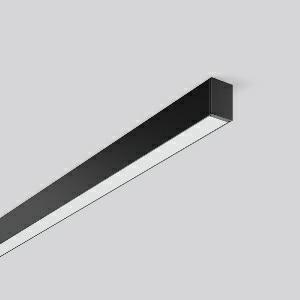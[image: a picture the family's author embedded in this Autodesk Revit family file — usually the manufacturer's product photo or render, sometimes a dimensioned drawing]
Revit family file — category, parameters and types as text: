
# Revit family: less_is_more_27_312197_003_76_2e7d
name_source: partatom
category: Lighting Fixtures
units: mm (PartAtom-declared; Revit-internal decimal feet)

## family parameters
Cut with Voids When Loaded = No
Host = Face
Light Source = No
Part Type = Normal
Room Calculation Point = No
Round Connector Dimension = Use Diameter
Shared = No

## types (1)
- LESS IS MORE 27 (1 x LED Modul 830, 1800 lm, 3000)
    Apparent Load = 29 VA
    CIE Flux Codes = 65 89 98 100 100
    Color Rendering = 80
    Color Temperature = 3000
    Default Elevation = 1800 mm  [stored 5.90551 ft]
    Description = Series: LESS IS MORE 27
Ceiling luminaire with slim design. Housing: extruded aluminium profile, powder-coated. End cap aluminium powder-coated. Diffuser made of non-yellowing plastic (PMMA) microprismatic. Suitable for Ceiling mounting, Wall (surface). External driver with connecting cable. 
Colour: deep black, matt (RAL 9005)
Length: 1012 mm
Width: 28 mm
Height: 38 mm
Lamp: LED
Socket: without socket
Colour temperature: 3000K
Colour rendering index (CRI): 82
System power: 29 W
Rated luminous flux: 1800 lm
Luminous efficiency: 62 lm/W
Control gear: Voltage converter, DALI dim.
Protection class: II
Type of protection: IP 20
    Height = 38 mm
    Lamp = 1 x LED Modul 830
    Lamp Light Flux = 1800 lm
    Lamp count = 1
    Length = 1012 mm
    Lifetime = 50000 h
    Luminous efficacy = 62 lm/W
    Manufacturer = RZB
    ModVariant = No
    Model = 312197.003.76
    Mounting Place = Ceiling, Wall
    Mounting Type = Surface mounted
    Number of Poles = 1
    OnlyDefault = Yes
    Power Factor = 1
    Product Name = LESS IS MORE 27
    Product group = Surface mounted LED linear luminaires
    ProductGroupID = 307
    Protection Class = Protection class II
    Protection Degree = IP 20
    RLX_Detail_Level = 1
    RLX_Emergency_Light_Flux = 0 lm
    RLX_Emergency_Type = 0
    RLX_Emergency_Type_DB = No
    RlxData = <blob elided: 29785 chars, md5=38d0541e>
    Socket = socket
    Standby Power = 0 W
    System Light Flux = 1800 lm
    System Power = 29 W
    Type Comments = Product without accessories
    Type Image = 312196.003.jpg
    URL = http://relux.com
    VarID = ---
    Voltage = 230 V
    Voltage Range = 220-240 V
    Weight = 0.00 kg
    Width = 28 mm

note: [stored X ft] marks values corroborated as IEEE doubles in the binary element streams (Revit-internal decimal feet)

## geometry (parser evidence)
native form markers: Blend x4, Sweep x10
no freeform markers — native parametric forms only
